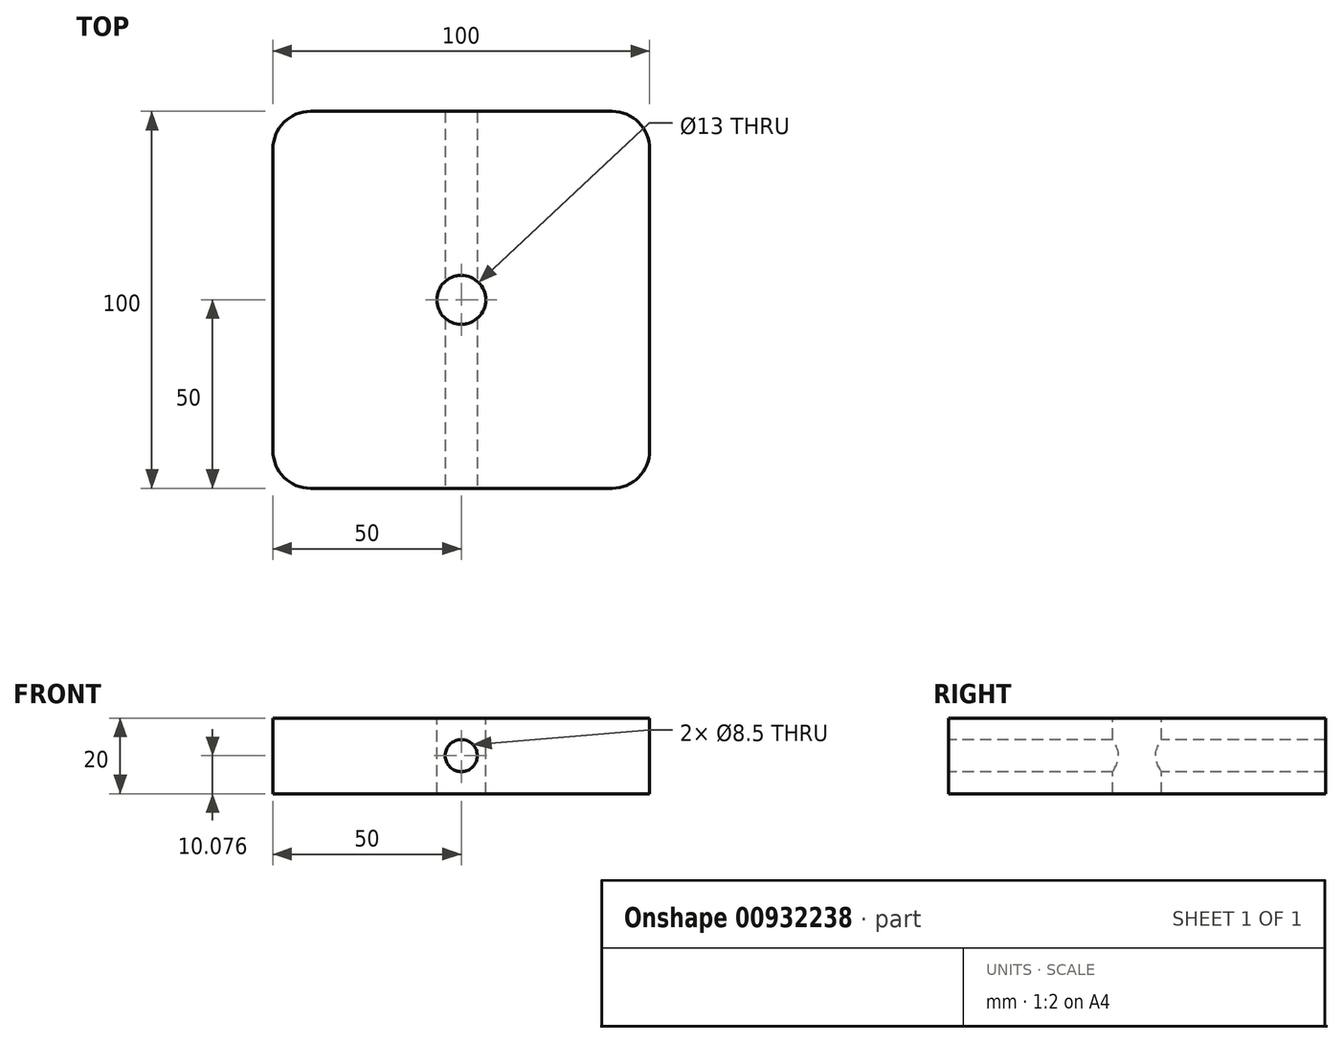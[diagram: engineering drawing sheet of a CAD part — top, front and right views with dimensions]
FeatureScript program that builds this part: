
annotation { "Feature Type Name" : "Feature", "Feature Type Description" : "" }
export const myFeature = defineFeature(function(context is Context, id is Id, definition is map)
    precondition{}
    {
        {
            var Q0;
            Q0=qCreatedBy(makeId("Top.planeOp"),FACE);
            var sketch = newSketch(context, id + "F0", { "sketchPlane" : qUnion([Q0])});
            skLineSegment(sketch, "E0.bottom", {"start": v(50, 50) * mm, "end": v(-50, 50) * mm});
            skLineSegment(sketch, "E0.top", {"start": v(50, -50) * mm, "end": v(-50, -50) * mm});
            skLineSegment(sketch, "E0.left", {"start": v(50, 50) * mm, "end": v(50, -50) * mm});
            skLineSegment(sketch, "E0.right", {"start": v(-50, 50) * mm, "end": v(-50, -50) * mm});
            skPoint(sketch, "E0.middle", {"position": v(0, 0) * mm});
            skPoint(sketch, "E1", {"position": v(0.12, -0.22) * mm});
            skSolve(sketch);
        }
        {
            var Q0;
            Q0=makeQuery(id+"F0.imprint","IMPRINT",FACE,{"disambiguationData":[TD([[makeQuery(id+"F0.imprint","IMPRINT",EDGE,{"derivedFrom":sQuery(id+"F0.wireOp",EDGE,"E0.bottom")}),1.0]])]});
            extrude(context, id + "F1", {"entities" : qUnion([Q0]), "depth" : 20 * mm, "offsetDistance" : 25.4 * mm});
        }
        {
            var Q0;
            Q0=makeQuery(id+"F1.opExtrude","SWEPT_FACE",FACE,{"disambiguationData":[OSD([sQuery(id+"F0.wireOp",EDGE,"E0.top")])]});
            var sketch = newSketch(context, id + "F2", { "sketchPlane" : qUnion([Q0])});
            skPoint(sketch, "E2", {"position": v(0, 0) * mm});
            skPoint(sketch, "E3", {"position": v(0, 10.08) * mm});
            skSolve(sketch);
        }
        {
            var Q0;
            Q0=sQuery(id+"F2.wireOp",VERTEX,"E3");
            var Q1;
            Q1=makeQuery(id+"F1.opExtrude","SWEPT_BODY",BODY,{"disambiguationData":[OSD([sQuery(id+"F0.wireOp",EDGE,"E0.bottom"),sQuery(id+"F0.wireOp",EDGE,"E0.top"),sQuery(id+"F0.wireOp",EDGE,"E0.left"),sQuery(id+"F0.wireOp",EDGE,"E0.right")])]});
            hole(context, id + "F3", {"style" : HoleStyle.SIMPLE, "endStyle" : HoleEndStyle.THROUGH, "standardTappedOrClearance" : lookupTablePath({ "standard" : "ISO", "size" : "8.5", "type" : "Drilled" }), "standardBlindInLast" : lookupTablePath({ "standard" : "ISO", "size" : "8.5", "type" : "Drilled" }), "holeDiameter" : 8.5 * mm, "majorDiameter" : 5 * mm, "isTappedThrough" : true, "tappedDepth" : 20 * mm, "tapClearance" : 3, "startFromSketch" : true, "locations" : qUnion([Q0]), "scope" : qUnion([Q1])});
        }
        {
            var Q0;
            Q0=makeQuery(id+"F1.opExtrude","CAP_FACE",FACE,{"disambiguationData":[OSD([sQuery(id+"F0.wireOp",EDGE,"E0.bottom"),sQuery(id+"F0.wireOp",EDGE,"E0.top"),sQuery(id+"F0.wireOp",EDGE,"E0.left"),sQuery(id+"F0.wireOp",EDGE,"E0.right")])],"isStart":false});
            var sketch = newSketch(context, id + "F4", { "sketchPlane" : qUnion([Q0])});
            skPoint(sketch, "E4", {"position": v(0, 0) * mm});
            skSolve(sketch);
        }
        {
            var Q0;
            Q0=sQuery(id+"F4.wireOp",VERTEX,"E4");
            var Q1;
            Q1=makeQuery(id+"F1.opExtrude","SWEPT_BODY",BODY,{"disambiguationData":[OSD([sQuery(id+"F0.wireOp",EDGE,"E0.bottom"),sQuery(id+"F0.wireOp",EDGE,"E0.top"),sQuery(id+"F0.wireOp",EDGE,"E0.left"),sQuery(id+"F0.wireOp",EDGE,"E0.right")])]});
            hole(context, id + "F5", {"style" : HoleStyle.SIMPLE, "endStyle" : HoleEndStyle.THROUGH, "standardTappedOrClearance" : lookupTablePath({ "standard" : "ISO", "size" : "13", "type" : "Drilled" }), "standardBlindInLast" : lookupTablePath({ "standard" : "ISO", "size" : "13", "type" : "Drilled" }), "holeDiameter" : 13 * mm, "majorDiameter" : 5 * mm, "isTappedThrough" : true, "tappedDepth" : 20 * mm, "tapClearance" : 3, "startFromSketch" : true, "locations" : qUnion([Q0]), "scope" : qUnion([Q1])});
        }
        {
            var Q0;
            Q0=makeQuery(id+"F1.opExtrude","SWEPT_EDGE",EDGE,{"disambiguationData":[OSD([sQuery(id+"F0.wireOp",EDGE,"E0.top"),sQuery(id+"F0.wireOp",EDGE,"E0.left")])]});
            var Q1;
            Q1=makeQuery(id+"F1.opExtrude","SWEPT_EDGE",EDGE,{"disambiguationData":[OSD([sQuery(id+"F0.wireOp",EDGE,"E0.top"),sQuery(id+"F0.wireOp",EDGE,"E0.right")])]});
            var Q2;
            Q2=makeQuery(id+"F1.opExtrude","SWEPT_EDGE",EDGE,{"disambiguationData":[OSD([sQuery(id+"F0.wireOp",EDGE,"E0.bottom"),sQuery(id+"F0.wireOp",EDGE,"E0.left")])]});
            var Q3;
            Q3=makeQuery(id+"F1.opExtrude","SWEPT_EDGE",EDGE,{"disambiguationData":[OSD([sQuery(id+"F0.wireOp",EDGE,"E0.bottom"),sQuery(id+"F0.wireOp",EDGE,"E0.right")])]});
            fillet(context, id + "F6", {"entities" : qUnion([Q0, Q1, Q2, Q3]), "radius" : 10 * mm, "tangentPropagation" : true, "allowEdgeOverflow" : false});
        }
    });
